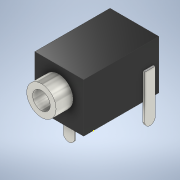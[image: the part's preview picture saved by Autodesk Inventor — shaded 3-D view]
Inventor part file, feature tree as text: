
AUTODESK INVENTOR PART (.ipt)
format: ipt  version: 2020 (Build 240168000, 168)  size: 202,752 bytes
history: native  units: mm
features: sketch x10, extrude x9, other x1, fillet x1
ambient origin geometry x8: Origin, YZ Plane, XZ Plane, XY Plane, X Axis, Y Axis, Z Axis, Center Point
bodies: Body1 (feature_tree)
feature tree (21):
  other  "Твердое тело1"
  extrude  "Выдавливание1"  Depth=15.4mm
  extrude  "Выдавливание2"  Depth=10.0mm
  extrude  "Выдавливание3"  Depth=10.0mm TaperAngle=0.0deg
  extrude  "Выдавливание4"  Depth=6.0mm
  extrude  "Выдавливание5"  Depth=5.5mm
  sketch  "Эскиз6"
  extrude  "Выдавливание6"  Depth=3.5mm TaperAngle=0.0deg
  extrude  "Выдавливание7"  Depth=3.6mm
  extrude  "Выдавливание8"  Depth=7.5mm TaperAngle=0.0deg
  extrude  "Выдавливание9"  Depth=0.3mm
  fillet  "Сопряжение1"  Radius=2.2mm
  sketch  "Эскиз1"
  sketch  "Эскиз2"
  sketch  "Эскиз3"
  sketch  "Эскиз4"
  sketch  "Эскиз5"
  sketch  "Эскиз7"
  sketch  "Эскиз8"
  sketch  "Эскиз9"
  sketch  "Эскиз10"
